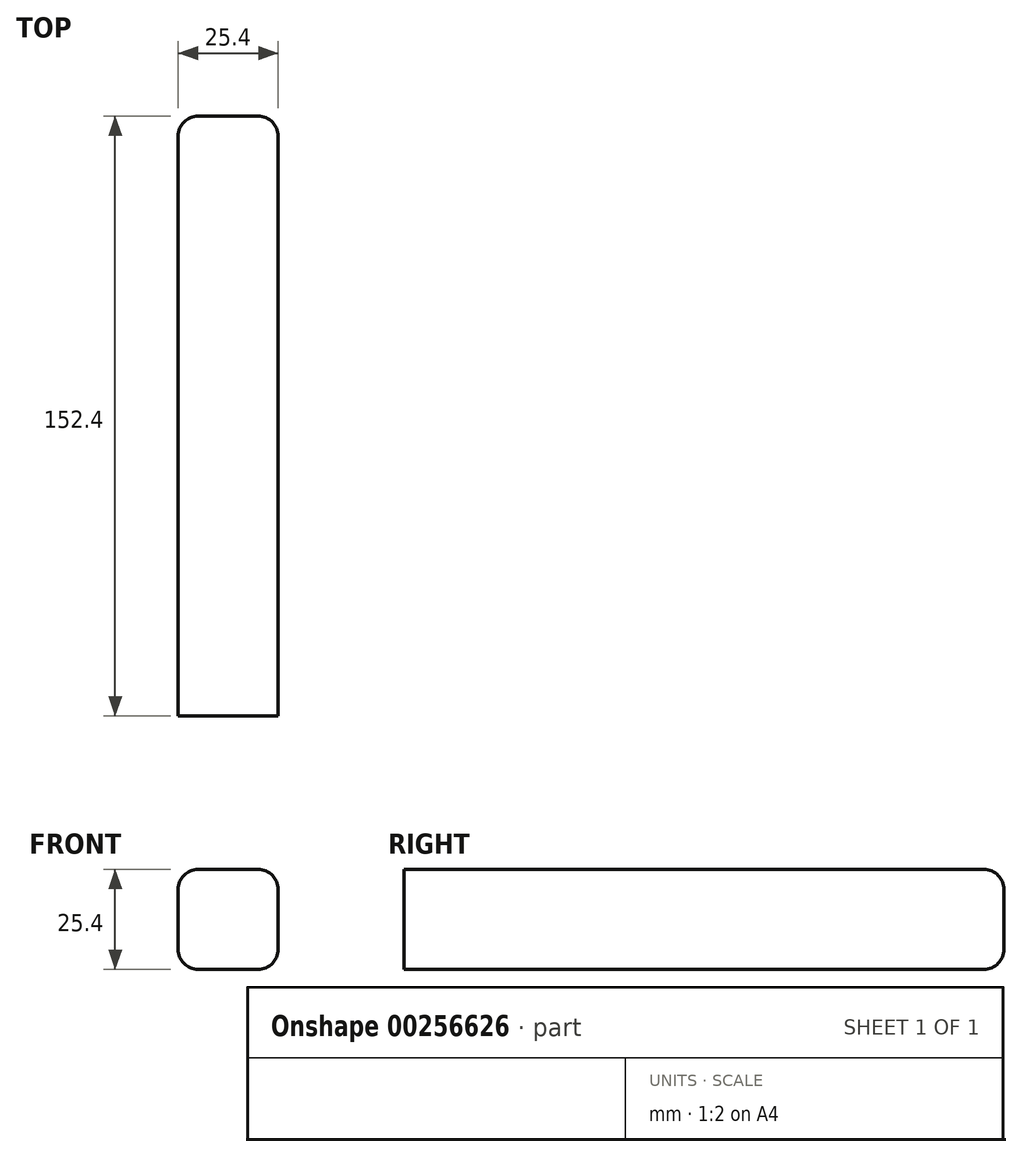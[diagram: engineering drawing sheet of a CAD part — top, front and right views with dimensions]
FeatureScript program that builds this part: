
annotation { "Feature Type Name" : "Feature", "Feature Type Description" : "" }
export const myFeature = defineFeature(function(context is Context, id is Id, definition is map)
    precondition{}
    {
        {
            var Q0;
            Q0=qCreatedBy(makeId("Front.planeOp"),FACE);
            var sketch = newSketch(context, id + "F0", { "sketchPlane" : qUnion([Q0])});
            skLineSegment(sketch, "E0.bottom", {"start": v(-12.7, -10.17) * mm, "end": v(12.7, -10.17) * mm});
            skLineSegment(sketch, "E0.top", {"start": v(-12.7, 15.23) * mm, "end": v(12.7, 15.23) * mm});
            skLineSegment(sketch, "E0.left", {"start": v(-12.7, -10.17) * mm, "end": v(-12.7, 15.23) * mm});
            skLineSegment(sketch, "E0.right", {"start": v(12.7, -10.17) * mm, "end": v(12.7, 15.23) * mm});
            skPoint(sketch, "E0.middle", {"position": v(0, 2.53) * mm});
            skSolve(sketch);
        }
        {
            var Q0;
            Q0 = qSketchRegion(id + "F0", true);
            extrude(context, id + "F1", {"entities" : qUnion([Q0]), "oppositeDirection" : true, "depth" : 152.4 * mm});
        }
        {
            var Q0;
            Q0=makeQuery(id+"F1.opExtrude","SWEPT_EDGE",EDGE,{"disambiguationData":[OSD([sQuery(id+"F0.wireOp",EDGE,"E0.bottom"),sQuery(id+"F0.wireOp",EDGE,"E0.left")])]});
            var Q1;
            Q1=makeQuery(id+"F1.opExtrude","SWEPT_EDGE",EDGE,{"disambiguationData":[OSD([sQuery(id+"F0.wireOp",EDGE,"E0.top"),sQuery(id+"F0.wireOp",EDGE,"E0.left")])]});
            var Q2;
            Q2=makeQuery(id+"F1.opExtrude","SWEPT_EDGE",EDGE,{"disambiguationData":[OSD([sQuery(id+"F0.wireOp",EDGE,"E0.bottom"),sQuery(id+"F0.wireOp",EDGE,"E0.right")])]});
            var Q3;
            Q3=makeQuery(id+"F1.opExtrude","SWEPT_EDGE",EDGE,{"disambiguationData":[OSD([sQuery(id+"F0.wireOp",EDGE,"E0.top"),sQuery(id+"F0.wireOp",EDGE,"E0.right")])]});
            var Q4;
            Q4=makeQuery(id+"F1.opExtrude","CAP_EDGE",EDGE,{"disambiguationData":[OSD([sQuery(id+"F0.wireOp",EDGE,"E0.left")])],"isStart":false});
            var Q5;
            Q5=makeQuery(id+"F1.opExtrude","CAP_EDGE",EDGE,{"disambiguationData":[OSD([sQuery(id+"F0.wireOp",EDGE,"E0.top")])],"isStart":false});
            var Q6;
            Q6=makeQuery(id+"F1.opExtrude","CAP_EDGE",EDGE,{"disambiguationData":[OSD([sQuery(id+"F0.wireOp",EDGE,"E0.right")])],"isStart":false});
            var Q7;
            Q7=makeQuery(id+"F1.opExtrude","CAP_EDGE",EDGE,{"disambiguationData":[OSD([sQuery(id+"F0.wireOp",EDGE,"E0.bottom")])],"isStart":false});
            fillet(context, id + "F2", {"entities" : qUnion([Q0, Q1, Q2, Q3, Q4, Q5, Q6, Q7]), "radius" : 5.08 * mm, "tangentPropagation" : true, "allowEdgeOverflow" : false});
        }
    });
